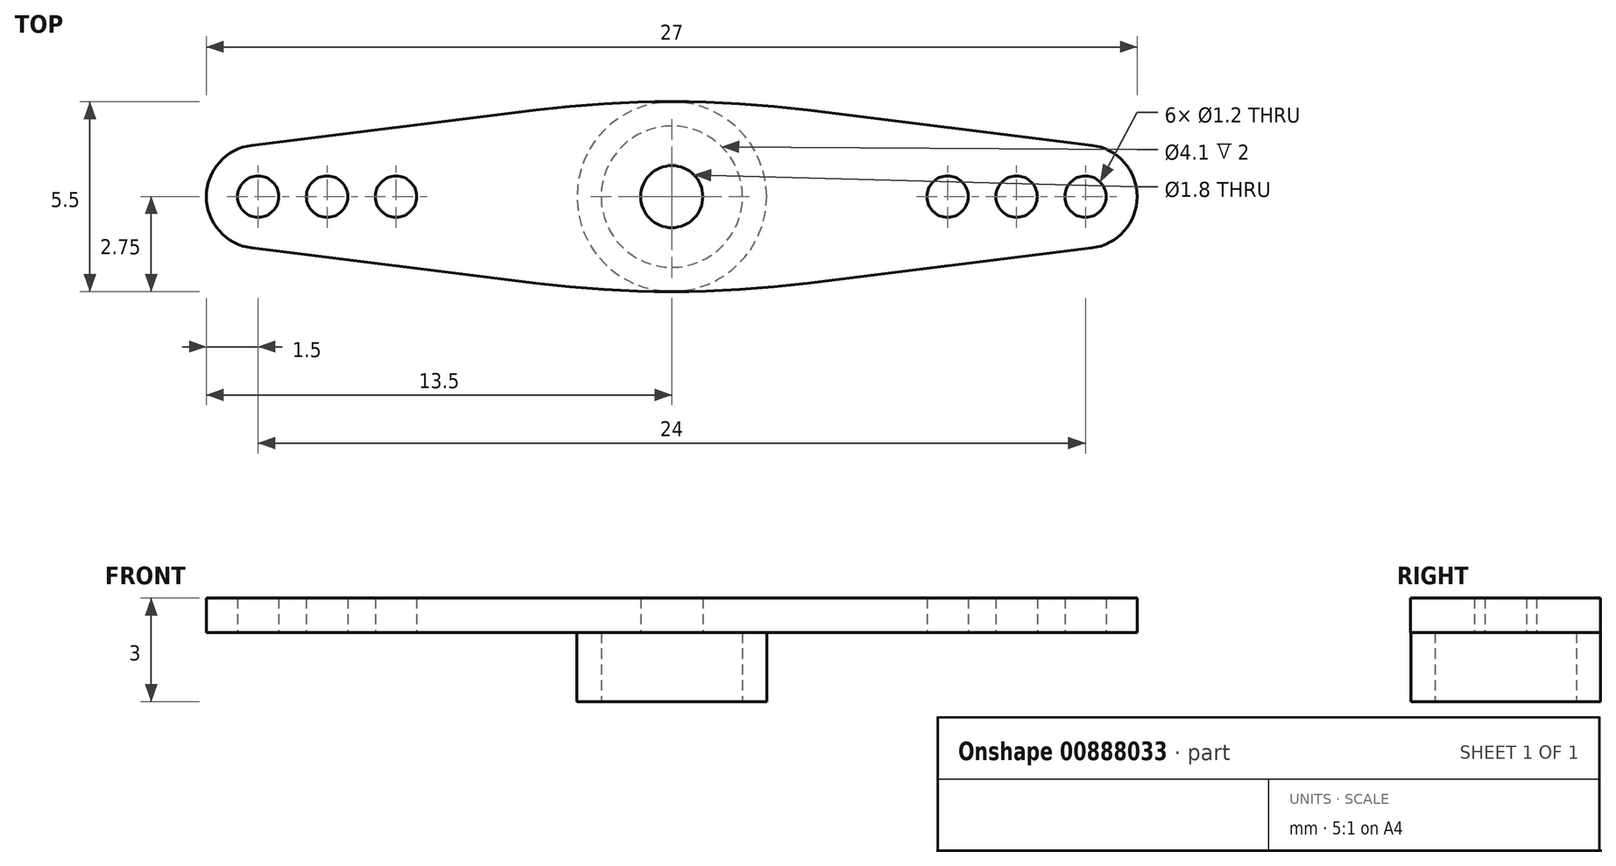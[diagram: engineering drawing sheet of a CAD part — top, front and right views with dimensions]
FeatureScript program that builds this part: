
annotation { "Feature Type Name" : "Feature", "Feature Type Description" : "" }
export const myFeature = defineFeature(function(context is Context, id is Id, definition is map)
    precondition{}
    {
        {
            var Q0;
            Q0=qCreatedBy(makeId("Top.planeOp"),FACE);
            var sketch = newSketch(context, id + "F0", { "sketchPlane" : qUnion([Q0])});
            skCircle(sketch, "E0", {"center": v(0, 0) * mm, "radius": 2.75 * mm});
            skCircle(sketch, "E1", {"center": v(0, 0) * mm, "radius": 2.05 * mm});
            skSolve(sketch);
        }
        {
            var Q0;
            Q0=qSketchRegion(id+"F0",true);
            extrude(context, id + "F1", {"entities" : qUnion([Q0]), "depth" : 2 * mm, "offsetDistance" : 25 * mm});
        }
        {
            var Q0;
            Q0=makeQuery(id+"F1.opExtrude","CAP_FACE",FACE,{"disambiguationData":[OSD([sQuery(id+"F0.wireOp",EDGE,"E0"),sQuery(id+"F0.wireOp",EDGE,"E1")])],"isStart":false});
            var sketch = newSketch(context, id + "F2", { "sketchPlane" : qUnion([Q0])});
            skLineSegment(sketch, "E2.left", {"start": v(13.5, 3) * mm, "end": v(13.5, -3) * mm});
            skPoint(sketch, "E2.middle", {"position": v(0, 0) * mm});
            skCircle(sketch, "E3", {"center": v(-12, 0) * mm, "radius": 1.5 * mm});
            skCircle(sketch, "E4", {"center": v(12, 0) * mm, "radius": 1.5 * mm});
            skLineSegment(sketch, "E5", {"start": v(0, 3) * mm, "end": v(-12.18, 1.49) * mm});
            skLineSegment(sketch, "E6", {"start": v(0, 3) * mm, "end": v(12.18, 1.49) * mm});
            skLineSegment(sketch, "E7", {"start": v(0, -3) * mm, "end": v(12.18, -1.49) * mm});
            skLineSegment(sketch, "E8", {"start": v(0, -3) * mm, "end": v(-12.18, -1.49) * mm});
            skCircle(sketch, "E9", {"center": v(12, 0) * mm, "radius": 0.6 * mm});
            skCircle(sketch, "E10", {"center": v(10, 0) * mm, "radius": 0.6 * mm});
            skCircle(sketch, "E11", {"center": v(8, 0) * mm, "radius": 0.6 * mm});
            skCircle(sketch, "E12", {"center": v(0, 0) * mm, "radius": 0.9 * mm});
            skCircle(sketch, "E13", {"center": v(-12, 0) * mm, "radius": 0.6 * mm});
            skCircle(sketch, "E14", {"center": v(-10, 0) * mm, "radius": 0.6 * mm});
            skCircle(sketch, "E15", {"center": v(-8, 0) * mm, "radius": 0.6 * mm});
            skSolve(sketch);
        }
        {
            var Q0;
            Q0=qSketchRegion(id+"F2",true);
            extrude(context, id + "F3", {"entities" : qUnion([Q0]), "operationType" : NewBodyOperationType.ADD, "depth" : 1 * mm, "offsetDistance" : 25 * mm});
        }
        {
            var Q0;
            Q0=makeQuery(id+"F3.opExtrude","SWEPT_EDGE",EDGE,{"disambiguationData":[OSD([sQuery(id+"F2.wireOp",EDGE,"E7"),sQuery(id+"F2.wireOp",EDGE,"E8")])]});
            fillet(context, id + "F4", {"entities" : qUnion([Q0]), "radius" : 32 * mm, "tangentPropagation" : true, "allowEdgeOverflow" : false});
        }
        {
            var Q0;
            Q0=makeQuery(id+"F3.opExtrude","SWEPT_EDGE",EDGE,{"disambiguationData":[OSD([sQuery(id+"F2.wireOp",EDGE,"E5"),sQuery(id+"F2.wireOp",EDGE,"E6")])]});
            fillet(context, id + "F5", {"entities" : qUnion([Q0]), "radius" : 32 * mm, "tangentPropagation" : true, "allowEdgeOverflow" : false});
        }
    });
